# Revit family: Gira_289600
name_source: partatom
category: Electrical Fixtures
revit_build: Autodesk Revit 2017 (Build: 20160225_1515(x64)
units: mm (PartAtom-declared; Revit-internal decimal feet)

## family parameters
Cut with Voids When Loaded = No
Host = Face
Maintain Annotation Orientation = No
Part Type = Normal
Room Calculation Point = No
Round Connector Dimension = Use Diameter
Shared = No

## types (1)
- Gerätedose 1f flach Gira E22
    Ausführung = sonstige
    Available = Yes
    Bauform = Gerätedose
    Befestigung der Geräte = schrauben
    Bestückung = ohne
    Category = Dose, Gehäuse für Montage in der Wand/Decke
    Data sheet (1) = https://katalog.gira.de
    Default Elevation = 1219 mm
    Form = quadratisch
    GTIN = 4010337066514
    HAN = 289600
    Halogenfrei = No
    HeinzeBIM = https://bimportal.heinze.de
    Keynote = E22flach_Gerätedose_1fach
    Manufacturer URL = https://www.gira.de
    Montageart = Hohlwand
    Name = Gerätedose 1f flach Gira E22
    Region = DE
    Schutzart (IP) = IP20
    URL = http://katalog.gira.de
    Werkstoff = Kunststoff

## geometry (parser evidence)
native form markers: Blend x2, Sweep x3
no freeform markers — native parametric forms only
